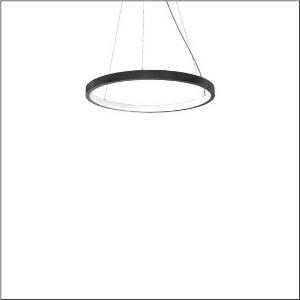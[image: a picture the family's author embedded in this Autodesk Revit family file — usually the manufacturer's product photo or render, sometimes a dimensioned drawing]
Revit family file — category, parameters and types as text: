
# Revit family: silica_r__21_ring-i_5pjbi2d1104a_14c4
name_source: partatom
category: Lighting Fixtures
units: mm (PartAtom-declared; Revit-internal decimal feet)

## family parameters
Cut with Voids When Loaded = No
Host = Face
Light Source = No
Part Type = Normal
Room Calculation Point = No
Round Connector Dimension = Use Diameter
Shared = No

## types (1)
- Silica® 21 Ring-I (1 x LED, 4800 lm, 80 W, 3000K)
    Apparent Load = 80 VA
    CIE Flux Codes = 22 48 76 50 101
    Color Rendering = 80
    Color Temperature = 3000K
    Default Elevation = 1800 mm
    Description = Silica® 21 Ring-I, suspended luminaire, of PMMA, frosted, light emission: inner ring side luminous distribution, primary light characteristic: symmetric, installation type: suspended mounting, LED, rated luminous flux: 4.800lm, luminous efficacy: 60lm/W, light colour: 830, colour temperature: 3000K, control gear: DALI 2, with terminal, 5-pole, mains connection: 230V, AC/DC, 0/50..60Hz, rated input power: 80W, housing, of extruded aluminium section, jet black (RAL 9005), diameter: 805mm, ceiling canopy, jet black (RAL 9005), protection rating (lamp compartment): IP40, insulation class (complete): insulation class I (protective earthing), certification: CE, impact resistance: IK02, permissible operating ambient temperature: 0..+35°C, packaging unit: 1 piece
    Height = 48 mm  [stored 0.15748 ft]
    Lamp = 1 x LED
    Lamp Light Flux = 4800 lm
    Lamp Power = 80 W
    Lamp count = 1
    Length = 805 mm
    Luminous efficacy = 60 lm/W
    Manufacturer = Siteco
    ModVariant = No
    Model = 5PJBI2D1104A
    Mounting Place = Ceiling
    Mounting Type = Pendant
    Number of Poles = 1
    OnlyDefault = Yes
    Power Factor = 1
    Product Name = Silica® 21 Ring-I
    Product group = suspended luminaire
    ProductGroupID = 905
    Protection Class = Protection class I
    Protection Degree = IP 40
    RLX_Detail_Level = 1
    RLX_Emergency_Light_Flux = 0 lm
    RLX_Emergency_Type = 0
    RLX_Emergency_Type_DB = No
    RlxData = <blob elided: 13949 chars, md5=7ca44ab0>
    Socket = socket
    Standby Power = 0 W
    System Light Flux = 4800 lm
    System Power = 80 W
    Type Comments = Product without accessories
    Type Image = l_1258365.jpg
    URL = http://relux.com
    VarID = ---
    Voltage = 0 V
    Weight = 0.00 kg
    Width = 0 mm  [stored 0 ft]

note: [stored X ft] marks values corroborated as IEEE doubles in the binary element streams (Revit-internal decimal feet)

## geometry (parser evidence)
native form markers: Sweep x13
no freeform markers — native parametric forms only
